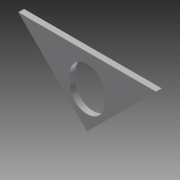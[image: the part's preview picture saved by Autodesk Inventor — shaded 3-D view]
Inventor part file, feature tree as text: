
AUTODESK INVENTOR PART (.ipt)
format: ipt  version: 2013 (Build 170138000, 138)  size: 83,456 bytes
history: native  units: in
note: dims shown in document units (in); Inventor stores cm internally (conversion verified against a paired STEP export)
features: extrude x2, sketch x2, plane x1
ambient origin geometry x8: Origin, YZ Plane, XZ Plane, XY Plane, X Axis, Y Axis, Z Axis, Center Point
bodies: Solid1 (feature_tree)
feature tree (5):
  extrude  "Extrusion1"  Depth=3.0in
  extrude  "Extrusion2"  Depth=0.4in
  plane  "Work Plane1"
  sketch  "Sketch1"  dims[d0=6.0in d2=3.0in]
  sketch  "Sketch2"  dims[d3=0.25in d4=0.0in d5=0.4in d6=0.75in d7=1.2in d8=0.25in d9=0.0in]
